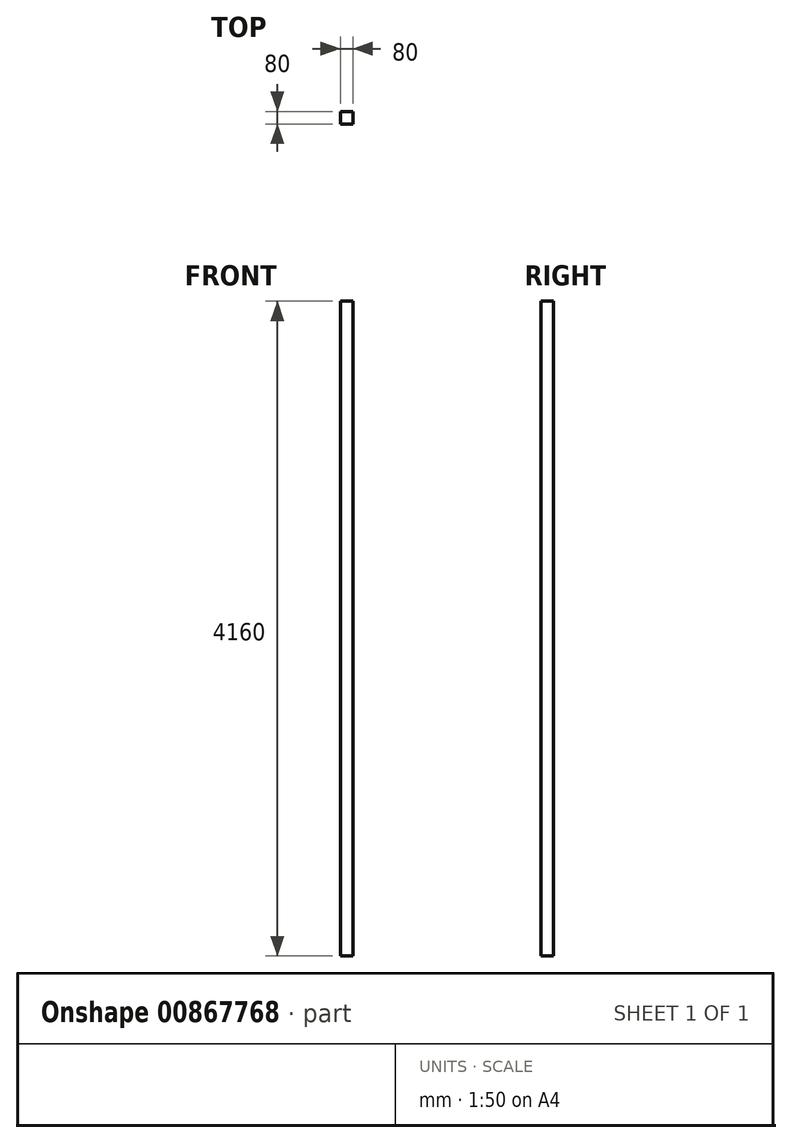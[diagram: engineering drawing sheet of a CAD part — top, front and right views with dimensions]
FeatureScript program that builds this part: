
annotation { "Feature Type Name" : "Feature", "Feature Type Description" : "" }
export const myFeature = defineFeature(function(context is Context, id is Id, definition is map)
    precondition{}
    {
        {
            var Q0;
            Q0=qCreatedBy(makeId("Top.planeOp"),FACE);
            var sketch = newSketch(context, id + "F0", { "sketchPlane" : qUnion([Q0])});
            skLineSegment(sketch, "E0.bottom", {"start": v(40, -40) * mm, "end": v(-40, -40) * mm});
            skLineSegment(sketch, "E0.top", {"start": v(40, 40) * mm, "end": v(-40, 40) * mm});
            skLineSegment(sketch, "E0.left", {"start": v(40, -40) * mm, "end": v(40, 40) * mm});
            skLineSegment(sketch, "E0.right", {"start": v(-40, -40) * mm, "end": v(-40, 40) * mm});
            skPoint(sketch, "E0.middle", {"position": v(0, 0) * mm});
            skSolve(sketch);
        }
        {
            var Q0;
            Q0=makeQuery(id+"F0.imprint","IMPRINT",FACE,{"disambiguationData":[TD([[makeQuery(id+"F0.imprint","IMPRINT",EDGE,{"derivedFrom":sQuery(id+"F0.wireOp",EDGE,"E0.bottom")}),-1.0]])]});
            extrude(context, id + "F1", {"entities" : qUnion([Q0]), "depth" : 4160 * mm, "offsetDistance" : 25 * mm});
        }
    });
